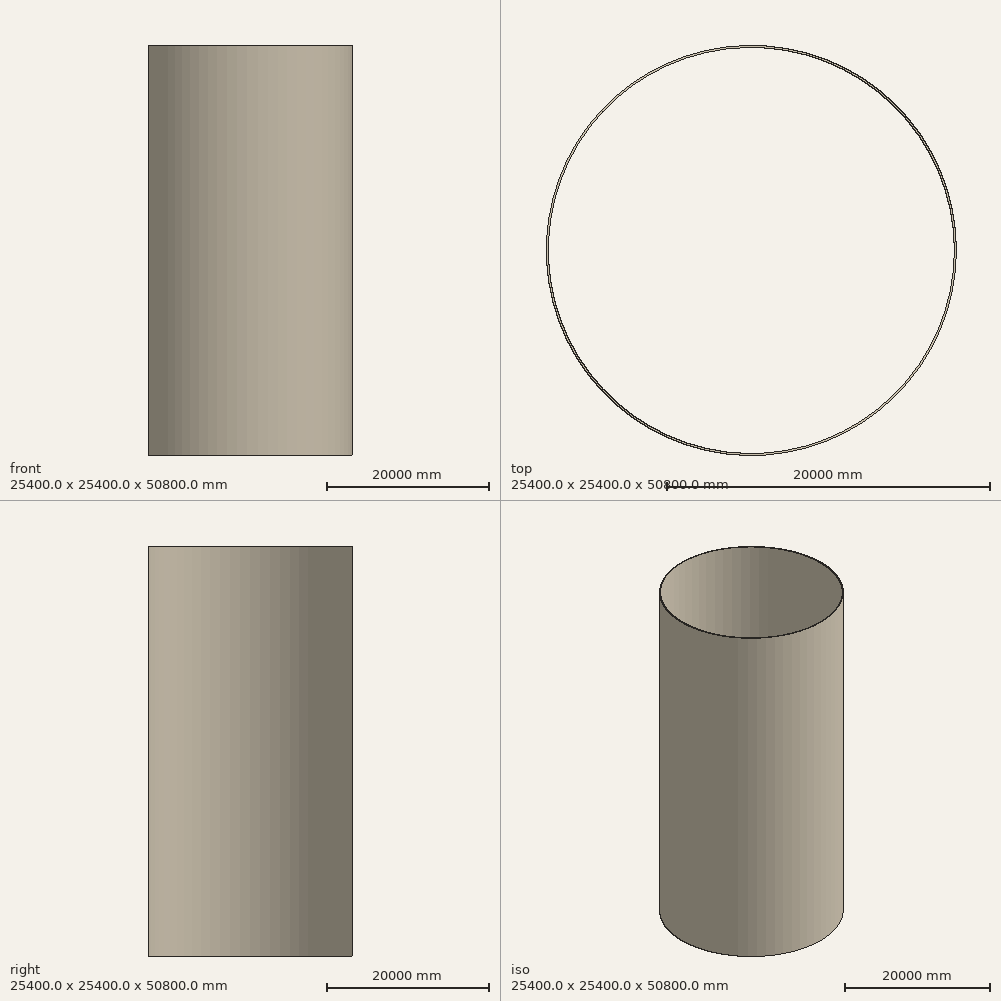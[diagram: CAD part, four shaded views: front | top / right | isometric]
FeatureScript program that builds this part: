
annotation { "Feature Type Name" : "Feature", "Feature Type Description" : "" }
export const myFeature = defineFeature(function(context is Context, id is Id, definition is map)
    precondition{}
    {
        {
            var Q0;
            Q0=qCreatedBy(makeId("Top.planeOp"),FACE);
            var sketch = newSketch(context, id + "F0", { "sketchPlane" : qUnion([Q0])});
            skCircle(sketch, "E0", {"center": v(0, 0) * mm, "radius": 12700 * mm});
            skCircle(sketch, "E1", {"center": v(0, 0) * mm, "radius": 12573 * mm});
            skSolve(sketch);
        }
        {
            var Q0;
            Q0=qSketchRegion(id+"F0",true);
            extrude(context, id + "F1", {"entities" : qUnion([Q0]), "depth" : 50800 * mm, "offsetDistance" : 25.4 * mm});
        }
    });
